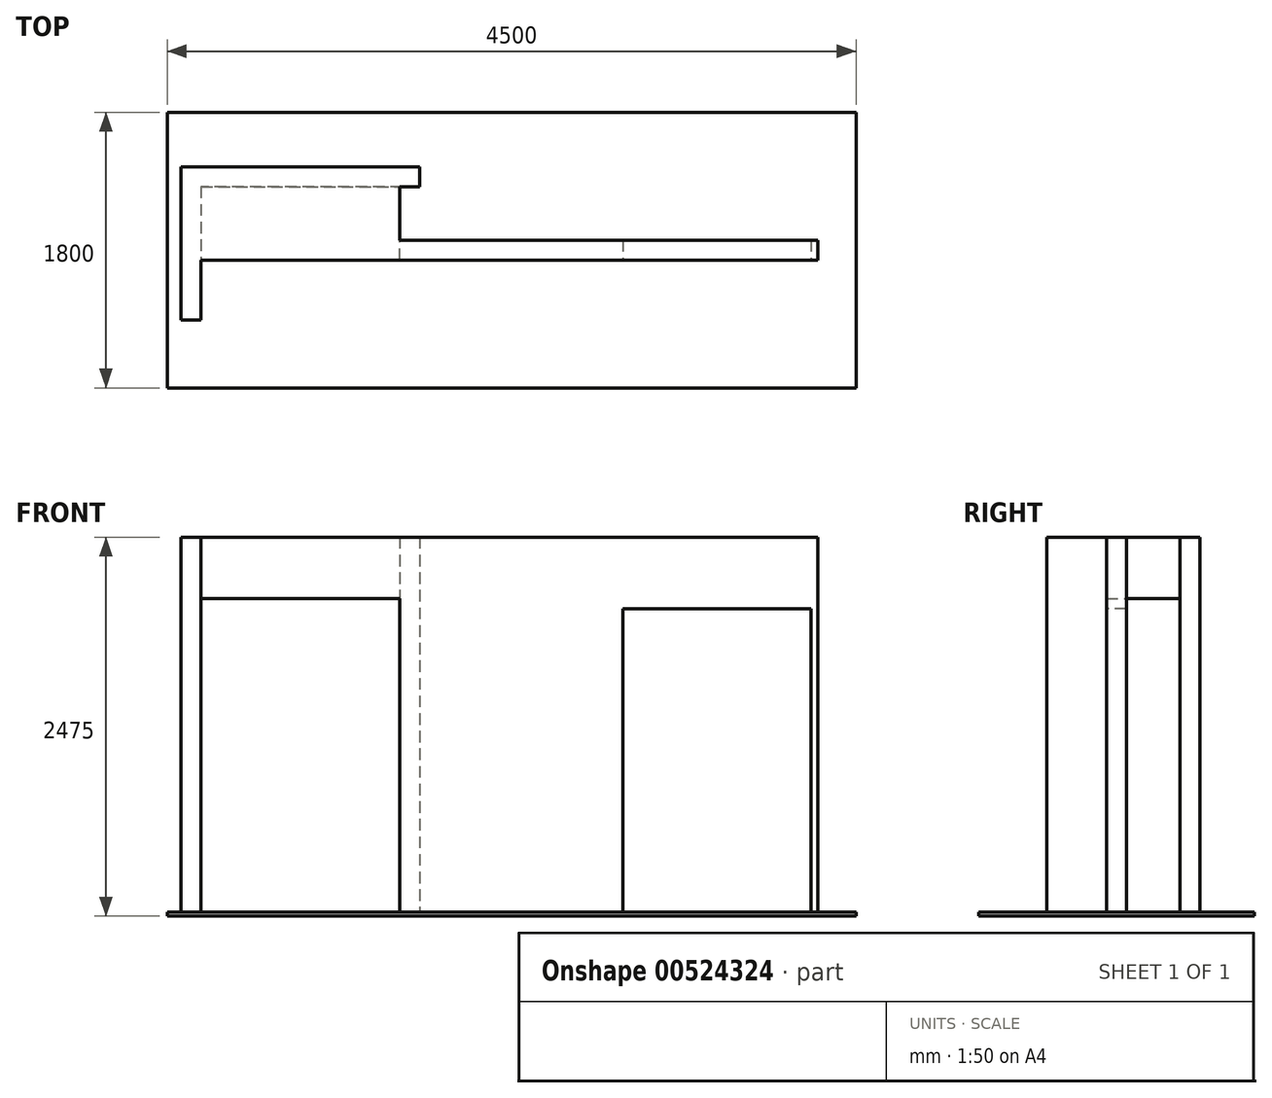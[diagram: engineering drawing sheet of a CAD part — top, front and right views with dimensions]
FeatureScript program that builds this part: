
annotation { "Feature Type Name" : "Feature", "Feature Type Description" : "" }
export const myFeature = defineFeature(function(context is Context, id is Id, definition is map)
    precondition{}
    {
        {
            var Q0;
            Q0=qCreatedBy(makeId("Top.planeOp"),FACE);
            var sketch = newSketch(context, id + "F0", { "sketchPlane" : qUnion([Q0])});
            skLineSegment(sketch, "E0.bottom", {"start": v(710, -65) * mm, "end": v(-710, -65) * mm});
            skLineSegment(sketch, "E0.top", {"start": v(710, 65) * mm, "end": v(-710, 65) * mm});
            skLineSegment(sketch, "E0.left", {"start": v(710, -65) * mm, "end": v(710, 65) * mm});
            skLineSegment(sketch, "E0.right", {"start": v(-710, -65) * mm, "end": v(-710, 65) * mm});
            skPoint(sketch, "E0.middle", {"position": v(0, 0) * mm});
            skLineSegment(sketch, "E1.bottom", {"start": v(710, -65) * mm, "end": v(2020, -65) * mm});
            skLineSegment(sketch, "E1.top", {"start": v(710, 65) * mm, "end": v(2020, 65) * mm});
            skLineSegment(sketch, "E1.right", {"start": v(2020, -65) * mm, "end": v(2020, 65) * mm});
            skLineSegment(sketch, "E2.bottom", {"start": v(-710, 65) * mm, "end": v(-580, 65) * mm});
            skLineSegment(sketch, "E2.top", {"start": v(-710, 415) * mm, "end": v(-580, 415) * mm});
            skLineSegment(sketch, "E2.left", {"start": v(-710, 65) * mm, "end": v(-710, 415) * mm});
            skLineSegment(sketch, "E2.right", {"start": v(-580, 65) * mm, "end": v(-580, 415) * mm});
            skLineSegment(sketch, "E3.bottom", {"start": v(-580, 415) * mm, "end": v(-2010, 415) * mm});
            skLineSegment(sketch, "E3.top", {"start": v(-580, 545) * mm, "end": v(-2010, 545) * mm});
            skLineSegment(sketch, "E3.left", {"start": v(-580, 415) * mm, "end": v(-580, 545) * mm});
            skLineSegment(sketch, "E3.right", {"start": v(-2010, 415) * mm, "end": v(-2010, 545) * mm});
            skLineSegment(sketch, "E4.bottom", {"start": v(-2010, 545) * mm, "end": v(-2140, 545) * mm});
            skLineSegment(sketch, "E4.top", {"start": v(-2010, -455) * mm, "end": v(-2140, -455) * mm});
            skLineSegment(sketch, "E4.left", {"start": v(-2010, 545) * mm, "end": v(-2010, -455) * mm});
            skLineSegment(sketch, "E4.right", {"start": v(-2140, 545) * mm, "end": v(-2140, -455) * mm});
            skSolve(sketch);
        }
        {
            var Q0;
            {var subQ3=sQuery(id+"F0.wireOp",EDGE,"E4.bottom");Q0=makeQuery(id+"F0.imprint","IMPRINT",FACE,{"disambiguationData":[TD([[makeQuery(id+"F0.imprint","IMPRINT",EDGE,{"derivedFrom":subQ3}),1.0]])]});}
            var Q1;
            {var subQ1=sQuery(id+"F0.wireOp",EDGE,"E3.top");Q1=makeQuery(id+"F0.imprint","IMPRINT",FACE,{"disambiguationData":[TD([[makeQuery(id+"F0.imprint","IMPRINT",EDGE,{"derivedFrom":subQ1}),1.0]])]});}
            var Q2;
            Q2=makeQuery(id+"F0.imprint","IMPRINT",FACE,{"disambiguationData":[TD([[makeQuery(id+"F0.imprint","IMPRINT",EDGE,{"derivedFrom":sQuery(id+"F0.wireOp",EDGE,"E2.bottom")}),1.0]])]});
            var Q3;
            Q3=makeQuery(id+"F0.imprint","IMPRINT",FACE,{"disambiguationData":[TD([[makeQuery(id+"F0.imprint","IMPRINT",EDGE,{"derivedFrom":sQuery(id+"F0.wireOp",EDGE,"E0.bottom")}),-1.0]])]});
            var Q4;
            Q4=makeQuery(id+"F0.imprint","IMPRINT",FACE,{"disambiguationData":[TD([[makeQuery(id+"F0.imprint","IMPRINT",EDGE,{"derivedFrom":sQuery(id+"F0.wireOp",EDGE,"E1.bottom")}),1.0]])]});
            extrude(context, id + "F1", {"entities" : qUnion([Q0, Q1, Q2, Q3, Q4]), "depth" : 2450 * mm, "offsetDistance" : 25 * mm});
        }
        {
            var Q0;
            Q0=makeQuery(id+"F1.opExtrude","CAP_FACE",FACE,{"disambiguationData":[OSD([sQuery(id+"F0.wireOp",EDGE,"E0.bottom"),sQuery(id+"F0.wireOp",EDGE,"E0.top"),sQuery(id+"F0.wireOp",EDGE,"E0.right"),sQuery(id+"F0.wireOp",EDGE,"E1.bottom"),sQuery(id+"F0.wireOp",EDGE,"E1.top"),sQuery(id+"F0.wireOp",EDGE,"E1.right"),sQuery(id+"F0.wireOp",EDGE,"E2.left"),sQuery(id+"F0.wireOp",EDGE,"E2.right"),sQuery(id+"F0.wireOp",EDGE,"E3.bottom"),sQuery(id+"F0.wireOp",EDGE,"E3.top"),sQuery(id+"F0.wireOp",EDGE,"E3.left"),sQuery(id+"F0.wireOp",EDGE,"E4.bottom"),sQuery(id+"F0.wireOp",EDGE,"E4.top"),sQuery(id+"F0.wireOp",EDGE,"E4.left"),sQuery(id+"F0.wireOp",EDGE,"E4.right")])],"isStart":false});
            var sketch = newSketch(context, id + "F2", { "sketchPlane" : qUnion([Q0])});
            skLineSegment(sketch, "E5.bottom", {"start": v(-2010, 415) * mm, "end": v(-710, 415) * mm});
            skLineSegment(sketch, "E5.top", {"start": v(-2010, -65) * mm, "end": v(-710, -65) * mm});
            skLineSegment(sketch, "E5.left", {"start": v(-2010, 415) * mm, "end": v(-2010, -65) * mm});
            skLineSegment(sketch, "E5.right", {"start": v(-710, 415) * mm, "end": v(-710, -65) * mm});
            skSolve(sketch);
        }
        {
            var Q0;
            Q0 = qSketchRegion(id + "F2", true);
            extrude(context, id + "F3", {"entities" : qUnion([Q0]), "operationType" : NewBodyOperationType.ADD, "oppositeDirection" : true, "depth" : 400 * mm, "offsetDistance" : 25 * mm});
        }
        {
            var Q0;
            Q0=makeQuery(id+"F3.boolean.opBoolean","MERGE",FACE,{"derivedFrom":[makeQuery(id+"F1.opExtrude","SWEPT_FACE",FACE,{"disambiguationData":[OSD([sQuery(id+"F0.wireOp",EDGE,"E0.bottom"),sQuery(id+"F0.wireOp",EDGE,"E1.bottom")])]}),makeQuery(id+"F3.opExtrude","SWEPT_FACE",FACE,{"disambiguationData":[OSD([sQuery(id+"F2.wireOp",EDGE,"E5.top")])]})]});
            var sketch = newSketch(context, id + "F4", { "sketchPlane" : qUnion([Q0])});
            skLineSegment(sketch, "E6.bottom", {"start": v(1975, 0) * mm, "end": v(745, 0) * mm});
            skLineSegment(sketch, "E6.top", {"start": v(1975, 1981) * mm, "end": v(745, 1981) * mm});
            skLineSegment(sketch, "E6.left", {"start": v(1975, 0) * mm, "end": v(1975, 1981) * mm});
            skLineSegment(sketch, "E6.right", {"start": v(745, 0) * mm, "end": v(745, 1981) * mm});
            skSolve(sketch);
        }
        {
            var Q0;
            Q0=makeQuery(id+"F4.imprint","IMPRINT",FACE,{"disambiguationData":[TD([[makeQuery(id+"F4.imprint","IMPRINT",EDGE,{"derivedFrom":sQuery(id+"F4.wireOp",EDGE,"E6.bottom")}),-1.0]])]});
            extrude(context, id + "F5", {"entities" : qUnion([Q0]), "operationType" : NewBodyOperationType.REMOVE, "endBound" : BoundingType.THROUGH_ALL, "oppositeDirection" : true, "depth" : 25 * mm, "offsetDistance" : 25 * mm});
        }
        {
            var Q0;
            Q0=qCreatedBy(makeId("Top.planeOp"),FACE);
            var sketch = newSketch(context, id + "F6", { "sketchPlane" : qUnion([Q0])});
            skLineSegment(sketch, "E7.bottom", {"start": v(2269.74, -900) * mm, "end": v(-2230.26, -900) * mm});
            skLineSegment(sketch, "E7.top", {"start": v(2269.74, 900) * mm, "end": v(-2230.26, 900) * mm});
            skLineSegment(sketch, "E7.left", {"start": v(2269.74, -900) * mm, "end": v(2269.74, 900) * mm});
            skLineSegment(sketch, "E7.right", {"start": v(-2230.26, -900) * mm, "end": v(-2230.26, 900) * mm});
            skPoint(sketch, "E7.middle", {"position": v(19.74, 0) * mm});
            skSolve(sketch);
        }
        {
            var Q0;
            Q0 = qSketchRegion(id + "F6", true);
            extrude(context, id + "F7", {"entities" : qUnion([Q0]), "oppositeDirection" : true, "depth" : 25 * mm, "offsetDistance" : 25 * mm});
        }
    });
